# Revit family: Basketball_Backstop-PSS-2350-Wall_Mounted
name_source: partatom
category: Specialty Equipment
revit_build: Autodesk Revit 2017 (Build: 20170816_0615(x64)
units: mm (PartAtom-declared; Revit-internal decimal feet)

## family parameters
Always vertical = Yes
Cut with Voids When Loaded = No
Host = Wall
OmniClass Number = 23.40.50.34.14.11
OmniClass Title = Backstops
Part Type = Normal
Room Calculation Point = No
Round Connector Dimension = Use Diameter
Shared = No

## types (1)
- 9124A
    Adjust A Goal = Yes
    Assembly Code = E1020900
    BIM Version = v3.1
    Backboard Fan Shaped = No
    Backboard Rectangular = Yes
    CSI MasterFormat = 11 66 23
    Description = Wall-Mounted, 3-Point Stationary Basketball Backstop
    Diagonal Brace Dim Front to Back = 2' - 8 7/8"
    Dim A Bottom Wall Attachment = 10' - 1 7/16"
    Dim B Middle Wall Attachment = 3' - 4 1/8"
    Dim C Top Wall Attachment = 6' - 7"
    Direct Attach Goal = No
    Installation Limitations = 9' to 12' Extension from Wall
    Large Steel Tubing Length = 6' - 6"
    Manufacturer = Performance Sports Systems
    Model = 2350
    Mounting Block Length = 6' - 0"
    Mounting Width = 5' - 3"
    Product Page URL = http://www.perfsports.com
    Superstructure Finish = Powder Coat - Performance Sports Systems - Black
    URL = http://www.perfsports.com

## geometry (parser evidence)
native form markers: Blend x41, Sweep x27
no freeform markers — native parametric forms only
